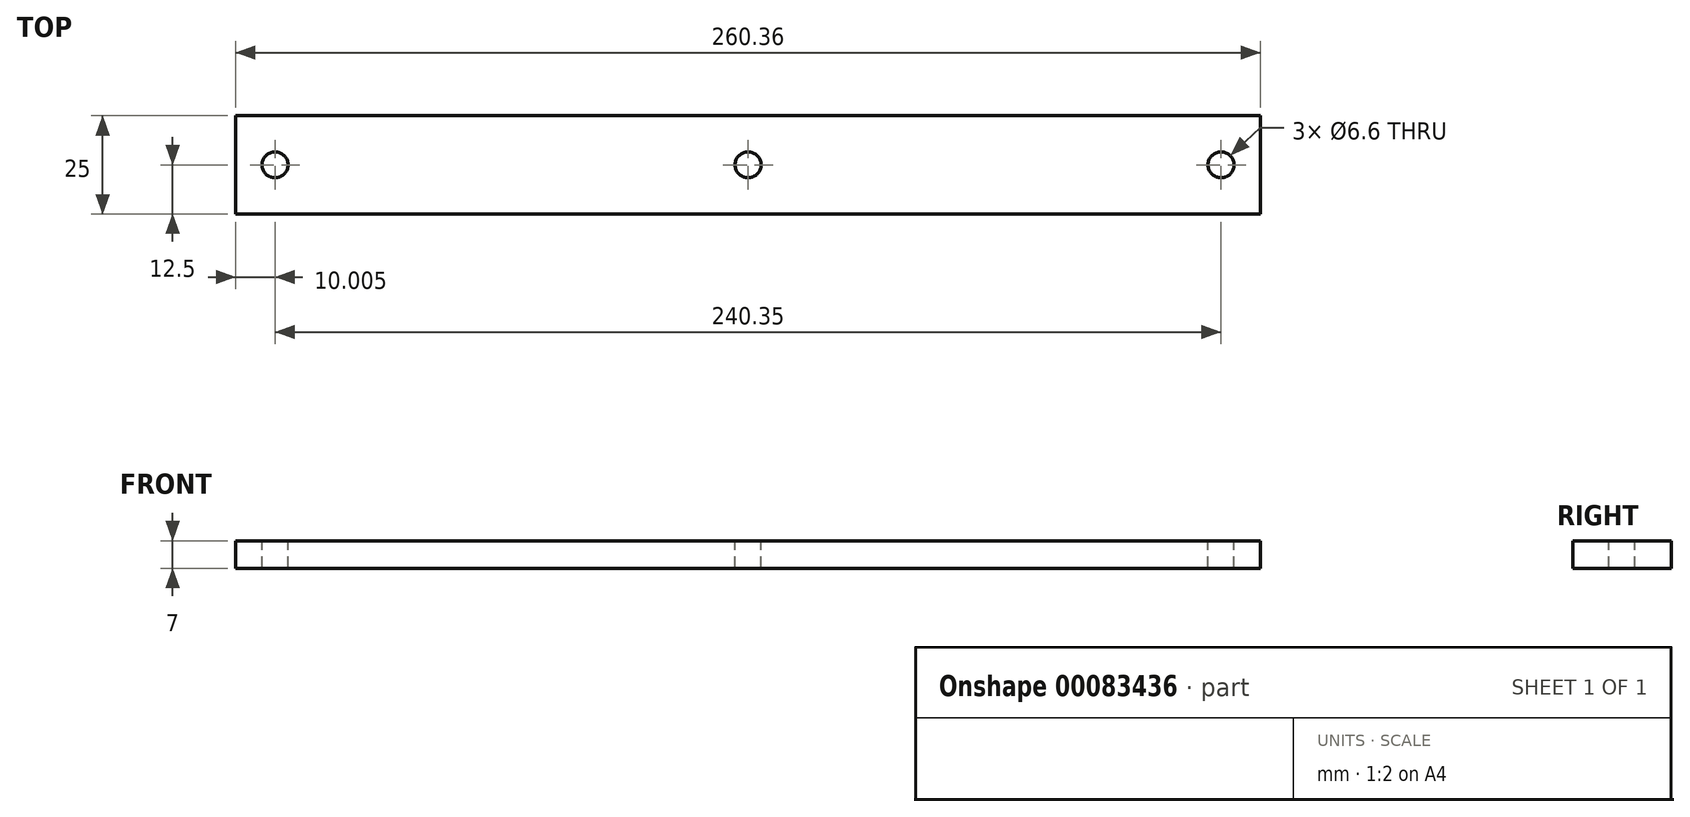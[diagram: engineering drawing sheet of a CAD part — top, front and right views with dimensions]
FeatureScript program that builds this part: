
annotation { "Feature Type Name" : "Feature", "Feature Type Description" : "" }
export const myFeature = defineFeature(function(context is Context, id is Id, definition is map)
    precondition{}
    {
        {
            var Q0;
            Q0=qCreatedBy(makeId("Top.planeOp"),FACE);
            var sketch = newSketch(context, id + "F0", { "sketchPlane" : qUnion([Q0])});
            skLineSegment(sketch, "E0.bottom", {"start": v(-130.18, 12.5) * mm, "end": v(130.18, 12.5) * mm});
            skLineSegment(sketch, "E0.top", {"start": v(-130.18, -12.5) * mm, "end": v(130.18, -12.5) * mm});
            skLineSegment(sketch, "E0.left", {"start": v(-130.18, 12.5) * mm, "end": v(-130.18, -12.5) * mm});
            skLineSegment(sketch, "E0.right", {"start": v(130.18, 12.5) * mm, "end": v(130.18, -12.5) * mm});
            skPoint(sketch, "E0.middle", {"position": v(0, 0) * mm});
            skSolve(sketch);
        }
        {
            var Q0;
            Q0 = qSketchRegion(id + "F0", true);
            extrude(context, id + "F1", {"entities" : qUnion([Q0]), "depth" : 7 * mm});
        }
        {
            var Q0;
            Q0=makeQuery(id+"F1.opExtrude","CAP_FACE",FACE,{"disambiguationData":[OSD([sQuery(id+"F0.wireOp",EDGE,"E0.bottom"),sQuery(id+"F0.wireOp",EDGE,"E0.top"),sQuery(id+"F0.wireOp",EDGE,"E0.left"),sQuery(id+"F0.wireOp",EDGE,"E0.right")])],"isStart":false});
            var sketch = newSketch(context, id + "F2", { "sketchPlane" : qUnion([Q0])});
            skLineSegment(sketch, "E1", {"start": v(-130.18, 0) * mm, "end": v(130.18, 0) * mm, "construction": true});
            skCircle(sketch, "E2", {"center": v(-120.18, 0) * mm, "radius": 3.3 * mm});
            skCircle(sketch, "E3", {"center": v(0, 0) * mm, "radius": 3.3 * mm});
            skCircle(sketch, "E4", {"center": v(120.18, 0) * mm, "radius": 3.3 * mm});
            skSolve(sketch);
        }
        {
            var Q0;
            Q0 = qSketchRegion(id + "F2", true);
            extrude(context, id + "F3", {"entities" : qUnion([Q0]), "operationType" : NewBodyOperationType.REMOVE, "endBound" : BoundingType.UP_TO_NEXT, "oppositeDirection" : true, "depth" : 25 * mm});
        }
    });
